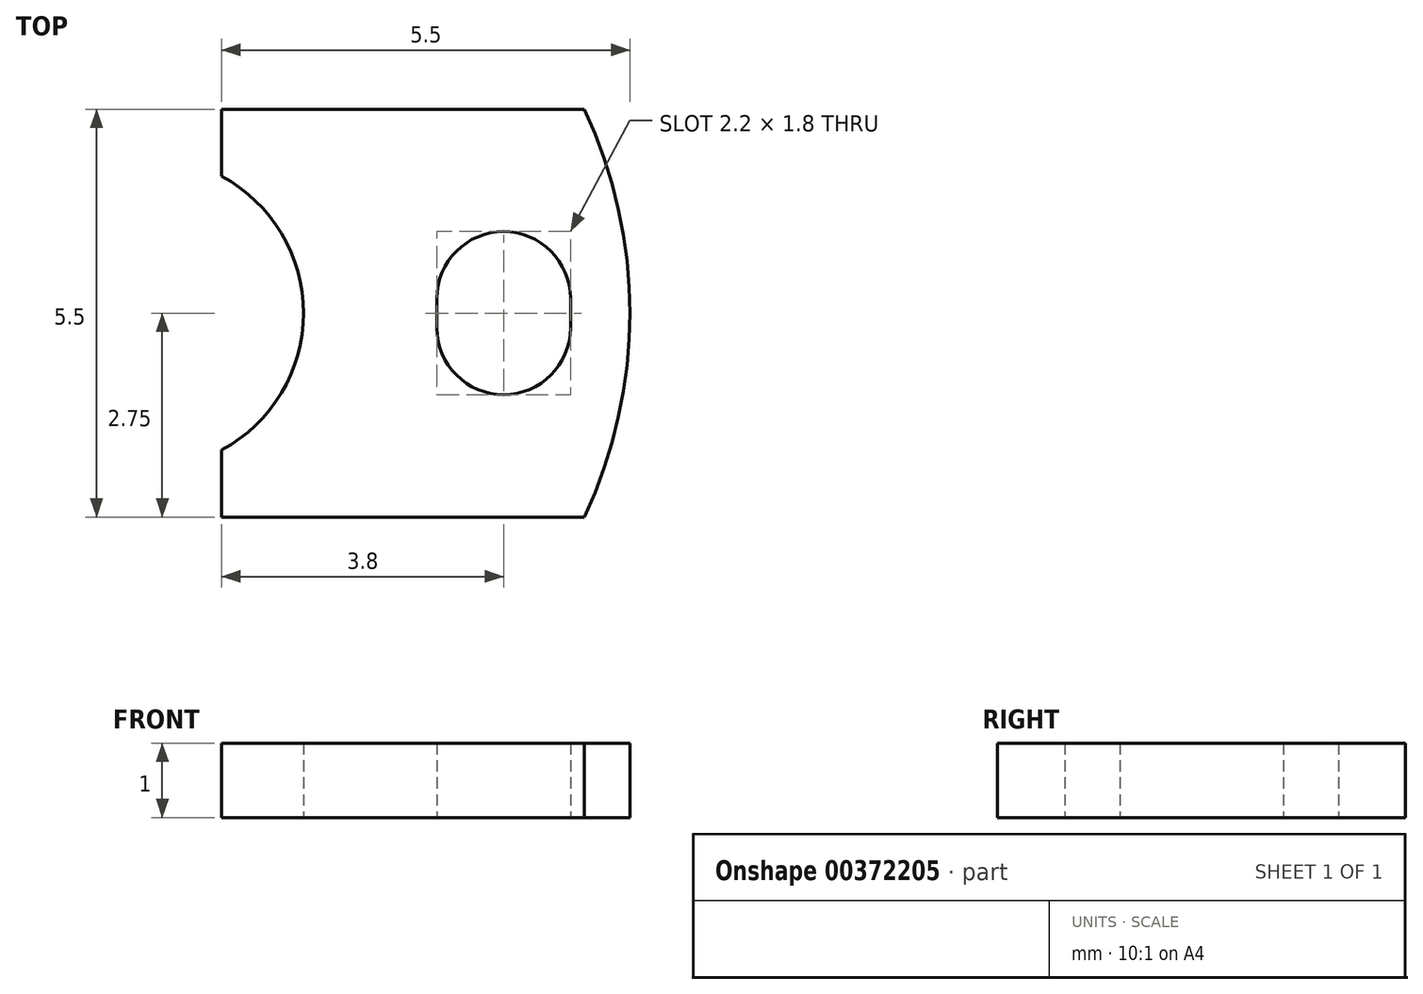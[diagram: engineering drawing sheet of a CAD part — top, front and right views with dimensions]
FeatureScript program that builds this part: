
annotation { "Feature Type Name" : "Feature", "Feature Type Description" : "" }
export const myFeature = defineFeature(function(context is Context, id is Id, definition is map)
    precondition{}
    {
        {
            var Q0;
            Q0=qCreatedBy(makeId("Top.planeOp"),FACE);
            var sketch = newSketch(context, id + "F0", { "sketchPlane" : qUnion([Q0])});
            skLineSegment(sketch, "E0.bottom", {"start": v(-3.8, 2.75) * mm, "end": v(1.09, 2.75) * mm});
            skLineSegment(sketch, "E0.top", {"start": v(-3.8, -2.75) * mm, "end": v(1.09, -2.75) * mm});
            skLineSegment(sketch, "E0.left", {"start": v(-3.8, 2.75) * mm, "end": v(-3.8, 1.85) * mm});
            skArc(sketch, "E1", {"start": v(1.09, -2.75) * mm, "mid": v(1.7, 0) * mm, "end": v(1.09, 2.75) * mm});
            skLineSegment(sketch, "E2.bottom", {"start": v(0, 1.1) * mm, "end": v(0, 1.1) * mm});
            skLineSegment(sketch, "E2.top", {"start": v(0, -1.1) * mm, "end": v(0, -1.1) * mm});
            skLineSegment(sketch, "E2.left", {"start": v(-0.9, 0.2) * mm, "end": v(-0.9, -0.2) * mm});
            skLineSegment(sketch, "E2.right", {"start": v(0.9, 0.2) * mm, "end": v(0.9, -0.2) * mm});
            skPoint(sketch, "E3.visualSharp", {"position": v(-0.9, 1.1) * mm});
            skArc(sketch, "E3.filletArc", {"start": v(0, 1.1) * mm, "mid": v(-0.64, 0.84) * mm, "end": v(-0.9, 0.2) * mm});
            skPoint(sketch, "E4.visualSharp", {"position": v(0.9, 1.1) * mm});
            skArc(sketch, "E4.filletArc", {"start": v(0.9, 0.2) * mm, "mid": v(0.64, 0.84) * mm, "end": v(0, 1.1) * mm});
            skPoint(sketch, "E5.visualSharp", {"position": v(0.9, -1.1) * mm});
            skArc(sketch, "E5.filletArc", {"start": v(0, -1.1) * mm, "mid": v(0.64, -0.84) * mm, "end": v(0.9, -0.2) * mm});
            skPoint(sketch, "E6.visualSharp", {"position": v(-0.9, -1.1) * mm});
            skArc(sketch, "E6.filletArc", {"start": v(-0.9, -0.2) * mm, "mid": v(-0.64, -0.84) * mm, "end": v(0, -1.1) * mm});
            skArc(sketch, "E7", {"start": v(-3.8, -1.85) * mm, "mid": v(-2.7, 0) * mm, "end": v(-3.8, 1.85) * mm});
            skLineSegment(sketch, "E8.trimOffspring", {"start": v(-3.8, -1.85) * mm, "end": v(-3.8, -2.75) * mm});
            skSolve(sketch);
        }
        {
            var Q0;
            Q0=makeQuery(id+"F0.imprint","IMPRINT",FACE,{"disambiguationData":[TD([[makeQuery(id+"F0.imprint","IMPRINT",EDGE,{"derivedFrom":sQuery(id+"F0.wireOp",EDGE,"E0.bottom")}),-1.0]])]});
            extrude(context, id + "F1", {"entities" : qUnion([Q0]), "depth" : 1 * mm});
        }
    });
